FCSTD DOCUMENT  (FreeCAD 0.19R24291 (Git))
Label: Problem 11
License: All rights reserved
LicenseURL: http://en.wikipedia.org/wiki/All_rights_reserved
objects: Part::Part2DObjectPython×20, App::FeaturePython×7
note: 20 computed .brp shape members not serialized (recipe doc carries the construction recipe); baked Part::Feature solids carry a one-line shape summary decoded from their .brp

FEATURE [Part::Part2DObjectPython] Line  # Draft 2D object (typed FeaturePython)
  Area = 0
  ChamferSize = 0
  Closed = true
  End = (-641.326,902.516,0)
  FilletRadius = 0
  Length = 300
  MakeFace = false
  Placement = pos=(-641.326,902.516,0) rot=(0,0,1;0rad)
  Points = (2) [(0,0,0),(0,0,0)]
  Start = (-641.326,902.516,0)
  Subdivisions = 0
FEATURE [Part::Part2DObjectPython] Rectangle003  # Draft 2D object (typed FeaturePython)
  Area = 0
  ChamferSize = 0
  Columns = 1
  FilletRadius = 0
  Height = 200
  Length = 200
  MakeFace = false
  Placement = pos=(-750.426,1111.62,0) rot=(0,0,1;0rad)
  Rows = 1
FEATURE [Part::Part2DObjectPython] Line001  # Draft 2D object (typed FeaturePython)
  Area = 0
  ChamferSize = 0
  Closed = false
  End = (-482.226,443.416,0)
  FilletRadius = 0
  Length = 225.001
  MakeFace = false
  Placement = pos=(-641.326,602.516,0) rot=(0,0,1;0rad)
  Points = (2) [(0,0,0),(159.1,-159.1,0)]
  Start = (-641.326,602.516,0)
  Subdivisions = 0
FEATURE [Part::Part2DObjectPython] Line002  # Draft 2D object (typed FeaturePython)
  Area = 0
  ChamferSize = 0
  Closed = false
  End = (-182.226,443.416,0)
  FilletRadius = 0
  Length = 225.001
  MakeFace = false
  Placement = pos=(-341.326,602.516,0) rot=(0,0,1;0rad)
  Points = (2) [(0,0,0),(159.1,-159.1,0)]
  Start = (-341.326,602.516,0)
  Subdivisions = 0
FEATURE [Part::Part2DObjectPython] Line003  # Draft 2D object (typed FeaturePython)
  Area = 0
  ChamferSize = 0
  Closed = false
  End = (-341.326,1202.52,0)
  FilletRadius = 0
  Length = 225.001
  MakeFace = false
  Placement = pos=(-182.226,1043.42,0) rot=(0,0,1;0rad)
  Points = (2) [(0,0,0),(-159.1,159.1,0)]
  Start = (-182.226,1043.42,0)
  Subdivisions = 0
FEATURE [Part::Part2DObjectPython] Line004  # Draft 2D object (typed FeaturePython)
  Area = 0
  ChamferSize = 0
  Closed = false
  End = (-641.326,902.516,0)
  FilletRadius = 0
  Length = 235.851
  MakeFace = false
  Placement = pos=(-750.426,1111.62,0) rot=(0,0,1;0rad)
  Points = (2) [(0,0,0),(109.1,-209.1,0)]
  Start = (-750.426,1111.62,0)
  Subdivisions = 0
FEATURE [Part::Part2DObjectPython] Line005  # Draft 2D object (typed FeaturePython)
  Area = 0
  ChamferSize = 0
  Closed = false
  End = (-344.483,905.673,0)
  FilletRadius = 0
  Length = 291.246
  MakeFace = false
  Placement = pos=(-550.426,1111.62,0) rot=(0,0,1;0rad)
  Points = (2) [(0,0,0),(205.942,-205.942,0)]
  Start = (-550.426,1111.62,0)
  Subdivisions = 0
FEATURE [Part::Part2DObjectPython] Line006  # Draft 2D object (typed FeaturePython)
  Area = 0
  ChamferSize = 0
  Closed = false
  End = (-341.326,1202.52,0)
  FilletRadius = 0
  Length = 235.851
  MakeFace = false
  Placement = pos=(-550.426,1311.62,0) rot=(0,0,1;0rad)
  Points = (2) [(0,0,0),(209.1,-109.1,0)]
  Start = (-550.426,1311.62,0)
  Subdivisions = 0
FEATURE [Part::Part2DObjectPython] Circle  # Draft 2D object (typed FeaturePython)
  Area = 0
  FirstAngle = 0
  LastAngle = 0
  MakeFace = false
  Placement = pos=(-650.426,1211.62,0) rot=(0,0,1;0rad)
  Radius = 50
FEATURE [Part::Part2DObjectPython] Circle001  # Draft 2D object (typed FeaturePython)
  Area = 0
  FirstAngle = 0
  LastAngle = 0
  MakeFace = false
  Placement = pos=(-544.356,1105.55,0) rot=(0,0,1;0rad)
  Radius = 50
FEATURE [Part::Part2DObjectPython] Line010  # Draft 2D object (typed FeaturePython)
  Area = 0
  ChamferSize = 0
  Closed = false
  End = (-579.711,1070.19,0)
  FilletRadius = 0
  Length = 150.006
  MakeFace = false
  Placement = pos=(-685.781,1176.26,0) rot=(0,0,1;0rad)
  Points = (2) [(0,0,0),(106.07,-106.07,0)]
  Start = (-685.781,1176.26,0)
  Subdivisions = 0
FEATURE [Part::Part2DObjectPython] Line009  # Draft 2D object (typed FeaturePython)
  Area = 0
  ChamferSize = 0
  Closed = false
  End = (-519.299,1151.2,0)
  FilletRadius = 0
  Length = 135.441
  MakeFace = false
  Placement = pos=(-615.07,1246.97,0) rot=(0,0,1;0rad)
  Points = (2) [(0,0,0),(95.7715,-95.7715,0)]
  Start = (-615.07,1246.97,0)
  Subdivisions = 0
FEATURE [App::FeaturePython] Dimension  # Draft dimension (typed FeaturePython)
  Diameter = false
  Dimline = (-223.946,348.719,0)
  Direction = (0,0,0)
  Distance = 300
  End = (-182.226,443.416,0)
  Normal = (0,0,1)
  Start = (-482.226,443.416,0)
FEATURE [App::FeaturePython] Dimension001  # Draft dimension (typed FeaturePython)
  Diameter = false
  Dimline = (-612.24,477.198,0)
  Direction = (0,0,0)
  Distance = 225.001
  End = (-641.326,602.516,0)
  Normal = (0,0,1)
  Start = (-482.226,443.416,0)
FEATURE [App::FeaturePython] Dimension002  # Draft dimension (typed FeaturePython)
  Diameter = false
  Dimline = (-875.843,1186.2,0)
  Direction = (0,0,0)
  Distance = 200
  End = (-750.426,1311.62,0)
  Normal = (0,0,1)
  Start = (-750.426,1111.62,0)
FEATURE [App::FeaturePython] Dimension003  # Draft dimension (typed FeaturePython)
  Diameter = false
  Dimline = (-80.0178,959.968,0)
  Direction = (0,0,0)
  Distance = 600
  End = (-182.226,1043.42,0)
  Normal = (0,0,1)
  Start = (-182.226,443.416,0)
FEATURE [App::FeaturePython] Dimension004  # Draft dimension (typed FeaturePython)
  Diameter = false
  Dimline = (-376.46,1343.49,0)
  Direction = (0,0,0)
  Distance = 450
  End = (-550.426,1311.62,0)
  Normal = (0,0,1)
  Start = (-232.227,993.418,0)
FEATURE [Part::Part2DObjectPython] Line013  # Draft 2D object (typed FeaturePython)
  Area = 0
  ChamferSize = 0
  Closed = false
  End = (-341.326,902.516,0)
  FilletRadius = 0
  Length = 300
  MakeFace = false
  Placement = pos=(-641.326,902.516,0) rot=(0,0,1;0rad)
  Points = (2) [(0,0,0),(300,0,0)]
  Start = (-641.326,902.516,0)
  Subdivisions = 0
FEATURE [Part::Part2DObjectPython] Line014  # Draft 2D object (typed FeaturePython)
  Area = 0
  ChamferSize = 0
  Closed = false
  End = (-641.326,902.516,0)
  FilletRadius = 0
  Length = 300
  MakeFace = false
  Placement = pos=(-641.326,602.516,0) rot=(0,0,1;0rad)
  Points = (2) [(0,0,0),(0,300,0)]
  Start = (-641.326,602.516,0)
  Subdivisions = 0
FEATURE [Part::Part2DObjectPython] Line015  # Draft 2D object (typed FeaturePython)
  Area = 0
  ChamferSize = 0
  Closed = false
  End = (-641.326,602.516,0)
  FilletRadius = 0
  Length = 300
  MakeFace = false
  Placement = pos=(-341.326,602.516,0) rot=(0,0,1;0rad)
  Points = (2) [(0,0,0),(-300,0,0)]
  Start = (-341.326,602.516,0)
  Subdivisions = 0
FEATURE [Part::Part2DObjectPython] Line016  # Draft 2D object (typed FeaturePython)
  Area = 0
  ChamferSize = 0
  Closed = false
  End = (-341.326,1202.52,0)
  FilletRadius = 0
  Length = 600
  MakeFace = false
  Placement = pos=(-341.326,602.516,0) rot=(0,0,1;0rad)
  Points = (2) [(0,0,0),(2.84217e-13,600,0)]
  Start = (-341.326,602.516,0)
  Subdivisions = 0
FEATURE [Part::Part2DObjectPython] Line017  # Draft 2D object (typed FeaturePython)
  Area = 0
  ChamferSize = 0
  Closed = false
  End = (-182.226,443.416,0)
  FilletRadius = 0
  Length = 300
  MakeFace = false
  Placement = pos=(-482.226,443.416,0) rot=(0,0,1;0rad)
  Points = (2) [(0,0,0),(300,0,0)]
  Start = (-482.226,443.416,0)
  Subdivisions = 0
FEATURE [Part::Part2DObjectPython] Line018  # Draft 2D object (typed FeaturePython)
  Area = 0
  ChamferSize = 0
  Closed = false
  End = (-182.226,1043.42,0)
  FilletRadius = 0
  Length = 600
  MakeFace = false
  Placement = pos=(-182.226,443.416,0) rot=(0,0,1;0rad)
  Points = (2) [(0,0,0),(2.84217e-14,600,0)]
  Start = (-182.226,443.416,0)
  Subdivisions = 0
FEATURE [Part::Part2DObjectPython] Line019  # Draft 2D object (typed FeaturePython)
  Area = 0
  ChamferSize = 0
  Closed = false
  End = (-650.426,1161.62,0)
  FilletRadius = 0
  Length = 100
  MakeFace = false
  Placement = pos=(-650.426,1261.62,0) rot=(0,0,1;0rad)
  Points = (2) [(0,0,0),(0,-100,0)]
  Start = (-650.426,1261.62,0)
  Subdivisions = 0
FEATURE [Part::Part2DObjectPython] Line020  # Draft 2D object (typed FeaturePython)
  Area = 0
  ChamferSize = 0
  Closed = false
  End = (-700.426,1211.62,0)
  FilletRadius = 0
  Length = 100
  MakeFace = false
  Placement = pos=(-600.426,1211.62,0) rot=(0,0,1;0rad)
  Points = (2) [(0,0,0),(-100,0,0)]
  Start = (-600.426,1211.62,0)
  Subdivisions = 0
FEATURE [App::FeaturePython] Text  # WARN: FeaturePython — macro-defined, semantics opaque (R4)
  Placement = pos=(86.4094,65.7015,0) rot=(1,0,0;1.5708rad)
  Text = All Dimensions are in mm
FEATURE [App::FeaturePython] dLabel  # WARN: FeaturePython — macro-defined, semantics opaque (R4)
  CustomText = Dia 100 | Depth 150
  LabelType = 0
  Placement = pos=(-730.042,1417.88,0) rot=(0,0,1;0rad)
  Points = (3) [(-730.042,1417.88,0),(-730.042,1366.42,0),(-678.109,1251.62,0)]
  StraightDirection = 1
  StraightDistance = -51.4631
  TargetPoint = (-678.109,1251.62,0)
  Text = Dia 100 | Depth 150
